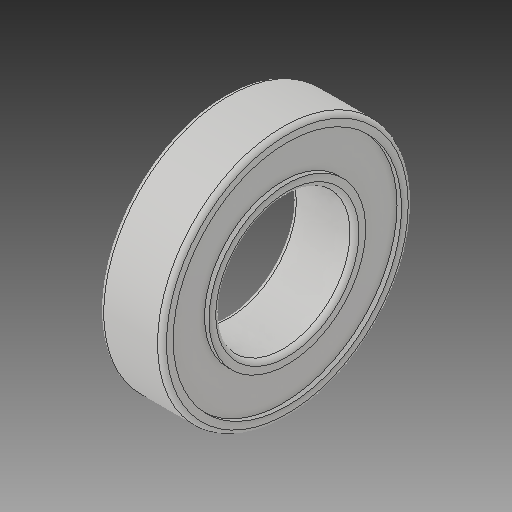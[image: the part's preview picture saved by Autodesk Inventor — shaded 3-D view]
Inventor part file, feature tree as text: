
AUTODESK INVENTOR PART (.ipt)
format: ipt  version: 2017 SP1 (Build 210196100, 196)  size: 176,128 bytes
history: native  units: in
note: dims shown in document units (in); Inventor stores cm internally (conversion verified against a paired STEP export)
features: fillet x1
ambient origin geometry x8: Origin, YZ Plane, XZ Plane, XY Plane, X Axis, Y Axis, Z Axis, Center Point
bodies: Solid1 (feature_tree)
feature tree (1):
  fillet  "Fillet1"  [1 undecoded]
note: 1 required parameter value undecoded (feature->parameter linkage not recoverable at this tier; creation-order binding heuristic only, values carry confidence <= 0.55)
